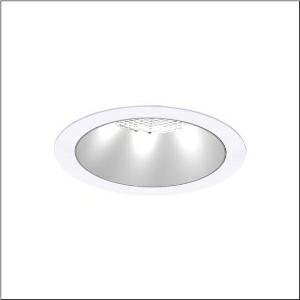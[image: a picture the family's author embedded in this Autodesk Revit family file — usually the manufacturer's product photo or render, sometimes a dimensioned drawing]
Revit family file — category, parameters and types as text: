
# Revit family: lunis_21_xl_51db19tf91c
name_source: partatom
category: Lighting Fixtures
units: mm (PartAtom-declared; Revit-internal decimal feet)

## family parameters
Cut with Voids When Loaded = No
Host = Face
Light Source = No
Part Type = Normal
Room Calculation Point = No
Round Connector Dimension = Use Diameter
Shared = No

## types (1)
- --- (1 x LED 3000 K ... 6500 K, 3940 lm, 25.4 W, 4000K)
    Apparent Load = 25 VA
    CIE Flux Codes = 91 99 100 100 100
    Color Rendering = 80
    Color Temperature = 4000K
    Default Elevation = 1800 mm
    Description = Lunis 21,  XL, downlight, light control with lens, of PMMA, anti glare with reflector, of aluminium, matt, light emission: direct distribution, LED rated luminous flux: 3.940lm, light colour: 8tw, with terminal, 5-pole, mains connection: 220..240V, AC/DC, 0/50..60Hz, housing, round, of diecast aluminium, traffic white (RAL 9016), diameter: 230mm, clamping range: 1..40mm, protection rating (complete): IP20, protection rating (on room side): IP54, insulation class (complete): insulation class II (safety insulation), certification: CE, impact resistance: IK03, packaging unit: 1 piece
    Height = 0 mm  [stored 0 ft]
    Lamp = 1 x LED 3000 K ... 6500 K
    Lamp Light Flux = 3940 lm
    Lamp Power = 25.4 W
    Lamp count = 1
    Length = 230 mm
    Luminous efficacy = 155 lm/W
    Manufacturer = Siteco
    ModVariant = No
    Model = 51DB19TF91C
    Mounting Place = Ceiling
    Mounting Type = Recessed
    Number of Poles = 1
    OnlyDefault = Yes
    Power Factor = 1
    Product Name = Lunis 21 XL
    Product group = downlight
    ProductGroupID = 400
    Protection Class = Protection class II
    Protection Degree = IP 20
    RLX_Detail_Level = 1
    RLX_Emergency_Light_Flux = 0 lm
    RLX_Emergency_Type = 0
    RLX_Emergency_Type_DB = No
    RlxData = <blob elided: 19601 chars, md5=52f5c572>
    Socket = socket
    Standby Power = 0 W
    System Light Flux = 3940 lm
    System Power = 25 W
    Type Comments = individual setting: CCT=4000K, colour temperature 4000K, luminous flux: 100 % | (ON | ON | OFF | OFF) | 700 mA
    Type Image = l_1291163.jpg
    URL = http://relux.com
    VarID = @adj_018692
    Voltage = 0 V
    Weight = 0.00 kg
    Width = 0 mm  [stored 0 ft]

note: [stored X ft] marks values corroborated as IEEE doubles in the binary element streams (Revit-internal decimal feet)

## geometry (parser evidence)
native form markers: Blend x4, Sweep x11
no freeform markers — native parametric forms only
